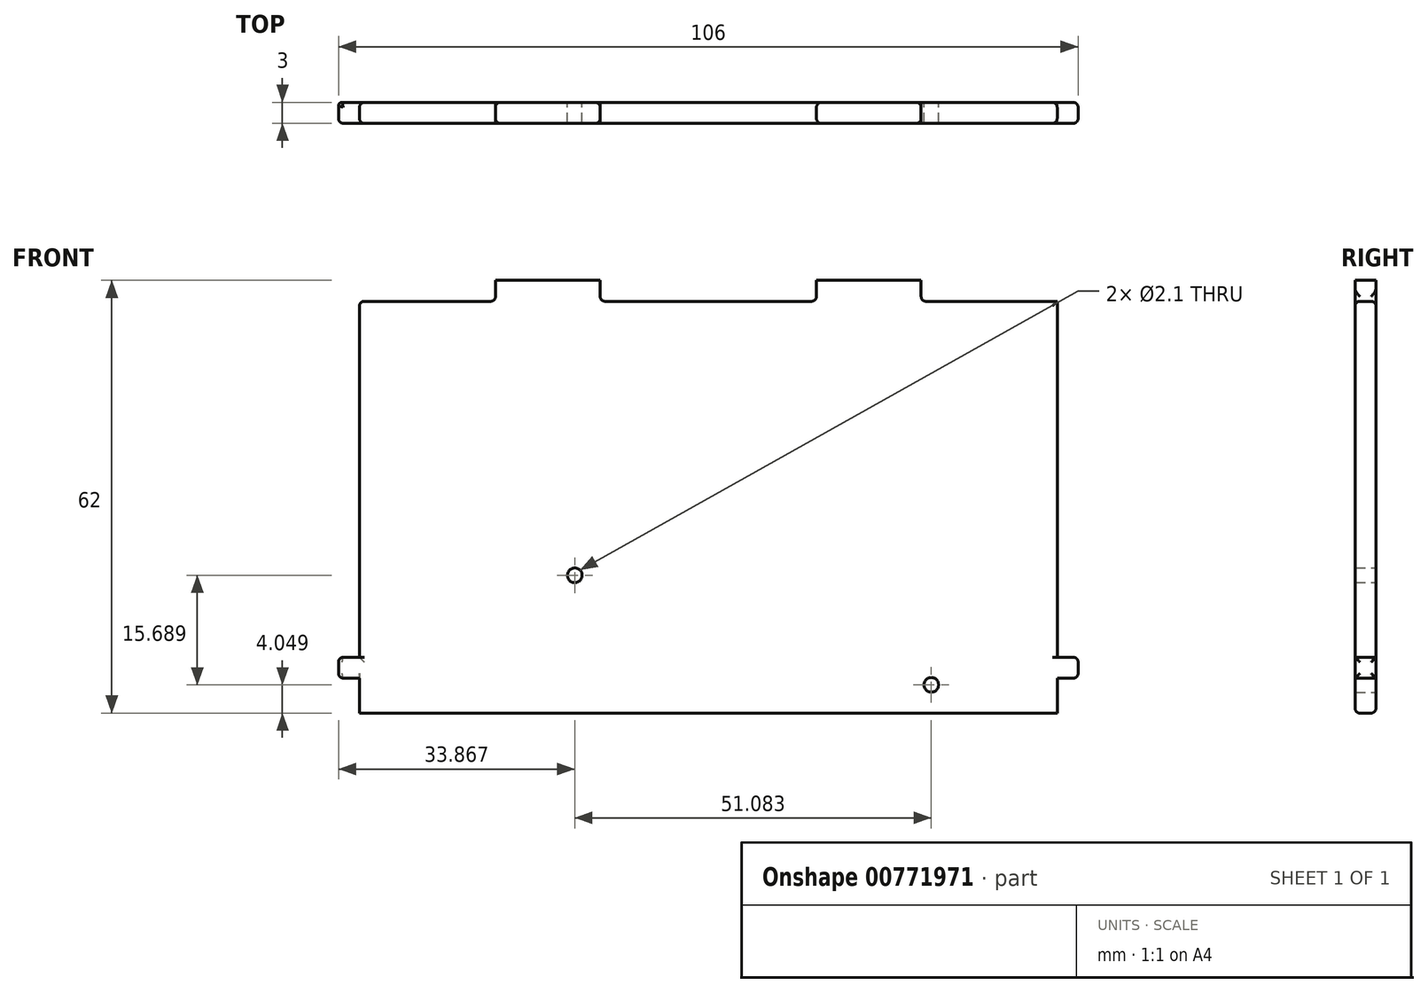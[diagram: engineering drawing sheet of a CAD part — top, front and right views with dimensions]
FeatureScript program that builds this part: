
annotation { "Feature Type Name" : "Feature", "Feature Type Description" : "" }
export const myFeature = defineFeature(function(context is Context, id is Id, definition is map)
    precondition{}
    {
        {
            var Q0;
            Q0=qCreatedBy(makeId("Front.planeOp"),FACE);
            var sketch = newSketch(context, id + "F0", { "sketchPlane" : qUnion([Q0])});
            skLineSegment(sketch, "E0.bottom", {"start": v(-50, -31.32) * mm, "end": v(50, -31.32) * mm});
            skLineSegment(sketch, "E0.top", {"start": v(-50, 27.68) * mm, "end": v(50, 27.68) * mm});
            skLineSegment(sketch, "E0.left", {"start": v(-50, -31.32) * mm, "end": v(-50, 27.68) * mm});
            skLineSegment(sketch, "E0.right", {"start": v(50, -31.32) * mm, "end": v(50, 27.68) * mm});
            skPoint(sketch, "E0.middle", {"position": v(0, -1.82) * mm});
            skLineSegment(sketch, "E1.bottom", {"start": v(-30.5, 27.68) * mm, "end": v(-15.5, 27.68) * mm});
            skLineSegment(sketch, "E1.top", {"start": v(-30.5, 30.68) * mm, "end": v(-15.5, 30.68) * mm});
            skLineSegment(sketch, "E1.left", {"start": v(-30.5, 27.68) * mm, "end": v(-30.5, 30.68) * mm});
            skLineSegment(sketch, "E1.right", {"start": v(-15.5, 27.68) * mm, "end": v(-15.5, 30.68) * mm});
            skLineSegment(sketch, "E2.bottom", {"start": v(30.5, 27.68) * mm, "end": v(15.5, 27.68) * mm});
            skLineSegment(sketch, "E2.top", {"start": v(30.5, 30.68) * mm, "end": v(15.5, 30.68) * mm});
            skLineSegment(sketch, "E2.left", {"start": v(30.5, 27.68) * mm, "end": v(30.5, 30.68) * mm});
            skLineSegment(sketch, "E2.right", {"start": v(15.5, 27.68) * mm, "end": v(15.5, 30.68) * mm});
            skLineSegment(sketch, "E3.bottom", {"start": v(-50, -23.32) * mm, "end": v(-53, -23.32) * mm});
            skLineSegment(sketch, "E3.top", {"start": v(-50, -26.32) * mm, "end": v(-53, -26.32) * mm});
            skLineSegment(sketch, "E3.left", {"start": v(-50, -23.32) * mm, "end": v(-50, -26.32) * mm});
            skLineSegment(sketch, "E3.right", {"start": v(-53, -23.32) * mm, "end": v(-53, -26.32) * mm});
            skLineSegment(sketch, "E4.bottom", {"start": v(50, -26.32) * mm, "end": v(53, -26.32) * mm});
            skLineSegment(sketch, "E4.top", {"start": v(50, -23.32) * mm, "end": v(53, -23.32) * mm});
            skLineSegment(sketch, "E4.left", {"start": v(50, -26.32) * mm, "end": v(50, -23.32) * mm});
            skLineSegment(sketch, "E4.right", {"start": v(53, -26.32) * mm, "end": v(53, -23.32) * mm});
            skCircle(sketch, "E5", {"center": v(31.95, -27.27) * mm, "radius": 1.05 * mm});
            skPoint(sketch, "E5.first.point", {"position": v(32.87, -27.78) * mm});
            skPoint(sketch, "E5.second.point", {"position": v(31.97, -26.22) * mm});
            skPoint(sketch, "E5.third.point", {"position": v(30.99, -27.7) * mm});
            skCircle(sketch, "E6", {"center": v(-19.13, -11.58) * mm, "radius": 1.05 * mm});
            skPoint(sketch, "E6.first.point", {"position": v(-20, -12.17) * mm});
            skPoint(sketch, "E6.second.point", {"position": v(-19.58, -12.53) * mm});
            skPoint(sketch, "E6.third.point", {"position": v(-18.39, -12.32) * mm});
            skSolve(sketch);
        }
        {
            var Q0;
            {var subQ7=sQuery(id+"F0.wireOp",EDGE,"E0.bottom");Q0=makeQuery(id+"F0.imprint","IMPRINT",FACE,{"disambiguationData":[TD([[makeQuery(id+"F0.imprint","IMPRINT",EDGE,{"derivedFrom":subQ7}),1.0]])]});}
            var Q1;
            {var subQ2=sQuery(id+"F0.wireOp",EDGE,"E4.bottom");Q1=makeQuery(id+"F0.imprint","IMPRINT",FACE,{"disambiguationData":[TD([[makeQuery(id+"F0.imprint","IMPRINT",EDGE,{"derivedFrom":subQ2}),1.0]])]});}
            var Q2;
            Q2=makeQuery(id+"F0.imprint","IMPRINT",FACE,{"disambiguationData":[TD([[makeQuery(id+"F0.imprint","IMPRINT",EDGE,{"derivedFrom":sQuery(id+"F0.wireOp",EDGE,"E2.top")}),1.0]])]});
            var Q3;
            Q3=makeQuery(id+"F0.imprint","IMPRINT",FACE,{"disambiguationData":[TD([[makeQuery(id+"F0.imprint","IMPRINT",EDGE,{"derivedFrom":sQuery(id+"F0.wireOp",EDGE,"E1.top")}),-1.0]])]});
            var Q4;
            {var subQ0=sQuery(id+"F0.wireOp",EDGE,"E3.bottom");Q4=makeQuery(id+"F0.imprint","IMPRINT",FACE,{"disambiguationData":[TD([[makeQuery(id+"F0.imprint","IMPRINT",EDGE,{"derivedFrom":subQ0}),1.0]])]});}
            extrude(context, id + "F1", {"entities" : qUnion([Q0, Q1, Q2, Q3, Q4]), "depth" : 3 * mm, "offsetDistance" : 25 * mm});
        }
        {
            var Q0;
            Q0=makeQuery(id+"F1.opExtrude","CAP_EDGE",EDGE,{"disambiguationData":[OSD([sQuery(id+"F0.wireOp",EDGE,"E3.right")])],"isStart":true});
            fillet(context, id + "F2", {"entities" : qUnion([Q0]), "radius" : 0.5 * mm, "tangentPropagation" : true, "allowEdgeOverflow" : false});
        }
        {
            var Q0;
            Q0=makeQuery(id+"F1.opExtrude","CAP_EDGE",EDGE,{"disambiguationData":[OSD([sQuery(id+"F0.wireOp",EDGE,"E3.right")])],"isStart":false});
            var Q1;
            Q1=makeQuery(id+"F1.opExtrude","SWEPT_EDGE",EDGE,{"disambiguationData":[OSD([sQuery(id+"F0.wireOp",EDGE,"E3.bottom"),sQuery(id+"F0.wireOp",EDGE,"E3.right")])]});
            var Q2;
            Q2=makeQuery(id+"F1.opExtrude","SWEPT_EDGE",EDGE,{"disambiguationData":[OSD([sQuery(id+"F0.wireOp",EDGE,"E3.top"),sQuery(id+"F0.wireOp",EDGE,"E3.right")])]});
            var Q3;
            {var subQ0=sQuery(id+"F0.wireOp",EDGE,"E3.right");Q3=makeQuery(id+"F2.opFillet","BLEND_EDGE",EDGE,{"blendedFrom":[makeQuery(id+"F1.opExtrude","CAP_EDGE",EDGE,{"disambiguationData":[OSD([subQ0])],"isStart":true}),makeQuery(id+"F1.opExtrude","SWEPT_FACE",FACE,{"disambiguationData":[OSD([subQ0])]})],"blendedInto":[makeQuery(id+"F1.opExtrude","SWEPT_FACE",FACE,{"disambiguationData":[OSD([subQ0])]})]});}
            var Q4;
            {var subQ0=sQuery(id+"F0.wireOp",EDGE,"E0.left");Q4=makeQuery(id+"F1.opExtrude","CAP_EDGE",EDGE,{"disambiguationData":[OSD([subQ0]),TDD([makeQuery(id+"F0.imprint","IMPRINT",EDGE,{"disambiguationData":[TD([[makeQuery(id+"F0.imprint","INTERSECT",VERTEX,{"derivedFrom":[subQ0,sQuery(id+"F0.wireOp",EDGE,"E3.bottom")]}),-1.0]])],"derivedFrom":subQ0})])],"isStart":true});}
            var Q5;
            {var subQ0=sQuery(id+"F0.wireOp",EDGE,"E0.left");Q5=makeQuery(id+"F1.opExtrude","CAP_EDGE",EDGE,{"disambiguationData":[OSD([subQ0]),TDD([makeQuery(id+"F0.imprint","IMPRINT",EDGE,{"disambiguationData":[TD([[makeQuery(id+"F0.imprint","INTERSECT",VERTEX,{"derivedFrom":[subQ0,sQuery(id+"F0.wireOp",EDGE,"E3.bottom")]}),-1.0]])],"derivedFrom":subQ0})])],"isStart":false});}
            var Q6;
            Q6=makeQuery(id+"F1.opExtrude","SWEPT_EDGE",EDGE,{"disambiguationData":[OSD([sQuery(id+"F0.wireOp",EDGE,"E0.top"),sQuery(id+"F0.wireOp",EDGE,"E0.left")])]});
            var Q7;
            {var subQ0=sQuery(id+"F0.wireOp",EDGE,"E0.top");Q7=makeQuery(id+"F1.opExtrude","CAP_EDGE",EDGE,{"disambiguationData":[OSD([subQ0]),TDD([makeQuery(id+"F0.imprint","IMPRINT",EDGE,{"disambiguationData":[TD([[makeQuery(id+"F0.imprint","INTERSECT",VERTEX,{"derivedFrom":[subQ0,sQuery(id+"F0.wireOp",EDGE,"E1.left")]}),1.0]])],"derivedFrom":subQ0})])],"isStart":true});}
            var Q8;
            {var subQ0=sQuery(id+"F0.wireOp",EDGE,"E0.top");Q8=makeQuery(id+"F1.opExtrude","CAP_EDGE",EDGE,{"disambiguationData":[OSD([subQ0]),TDD([makeQuery(id+"F0.imprint","IMPRINT",EDGE,{"disambiguationData":[TD([[makeQuery(id+"F0.imprint","INTERSECT",VERTEX,{"derivedFrom":[subQ0,sQuery(id+"F0.wireOp",EDGE,"E1.left")]}),1.0]])],"derivedFrom":subQ0})])],"isStart":false});}
            var Q9;
            Q9=makeQuery(id+"F1.opExtrude","SWEPT_EDGE",EDGE,{"disambiguationData":[OSD([sQuery(id+"F0.wireOp",EDGE,"E0.top"),sQuery(id+"F0.wireOp",EDGE,"E1.left")])]});
            var Q10;
            Q10=makeQuery(id+"F1.opExtrude","SWEPT_EDGE",EDGE,{"disambiguationData":[OSD([sQuery(id+"F0.wireOp",EDGE,"E0.top"),sQuery(id+"F0.wireOp",EDGE,"E1.right")])]});
            var Q11;
            {var subQ0=sQuery(id+"F0.wireOp",EDGE,"E0.top");Q11=makeQuery(id+"F1.opExtrude","CAP_EDGE",EDGE,{"disambiguationData":[OSD([subQ0]),TDD([makeQuery(id+"F0.imprint","IMPRINT",EDGE,{"disambiguationData":[TD([[makeQuery(id+"F0.imprint","INTERSECT",VERTEX,{"derivedFrom":[subQ0,sQuery(id+"F0.wireOp",EDGE,"E1.right")]}),-1.0]])],"derivedFrom":subQ0})])],"isStart":true});}
            var Q12;
            {var subQ0=sQuery(id+"F0.wireOp",EDGE,"E0.top");Q12=makeQuery(id+"F1.opExtrude","CAP_EDGE",EDGE,{"disambiguationData":[OSD([subQ0]),TDD([makeQuery(id+"F0.imprint","IMPRINT",EDGE,{"disambiguationData":[TD([[makeQuery(id+"F0.imprint","INTERSECT",VERTEX,{"derivedFrom":[subQ0,sQuery(id+"F0.wireOp",EDGE,"E1.right")]}),-1.0]])],"derivedFrom":subQ0})])],"isStart":false});}
            var Q13;
            {var subQ0=sQuery(id+"F0.wireOp",EDGE,"E0.top");Q13=makeQuery(id+"F1.opExtrude","CAP_EDGE",EDGE,{"disambiguationData":[OSD([subQ0]),TDD([makeQuery(id+"F0.imprint","IMPRINT",EDGE,{"disambiguationData":[TD([[makeQuery(id+"F0.imprint","INTERSECT",VERTEX,{"derivedFrom":[subQ0,sQuery(id+"F0.wireOp",EDGE,"E2.left")]}),-1.0]])],"derivedFrom":subQ0})])],"isStart":false});}
            var Q14;
            {var subQ0=sQuery(id+"F0.wireOp",EDGE,"E0.top");Q14=makeQuery(id+"F1.opExtrude","CAP_EDGE",EDGE,{"disambiguationData":[OSD([subQ0]),TDD([makeQuery(id+"F0.imprint","IMPRINT",EDGE,{"disambiguationData":[TD([[makeQuery(id+"F0.imprint","INTERSECT",VERTEX,{"derivedFrom":[subQ0,sQuery(id+"F0.wireOp",EDGE,"E2.left")]}),-1.0]])],"derivedFrom":subQ0})])],"isStart":true});}
            var Q15;
            Q15=makeQuery(id+"F1.opExtrude","SWEPT_EDGE",EDGE,{"disambiguationData":[OSD([sQuery(id+"F0.wireOp",EDGE,"E0.top"),sQuery(id+"F0.wireOp",EDGE,"E2.left")])]});
            var Q16;
            {var subQ0=sQuery(id+"F0.wireOp",EDGE,"E0.right");Q16=makeQuery(id+"F1.opExtrude","CAP_EDGE",EDGE,{"disambiguationData":[OSD([subQ0]),TDD([makeQuery(id+"F0.imprint","IMPRINT",EDGE,{"disambiguationData":[TD([[makeQuery(id+"F0.imprint","INTERSECT",VERTEX,{"derivedFrom":[subQ0,sQuery(id+"F0.wireOp",EDGE,"E4.top")]}),-1.0]])],"derivedFrom":subQ0})])],"isStart":false});}
            var Q17;
            {var subQ0=sQuery(id+"F0.wireOp",EDGE,"E0.right");Q17=makeQuery(id+"F1.opExtrude","CAP_EDGE",EDGE,{"disambiguationData":[OSD([subQ0]),TDD([makeQuery(id+"F0.imprint","IMPRINT",EDGE,{"disambiguationData":[TD([[makeQuery(id+"F0.imprint","INTERSECT",VERTEX,{"derivedFrom":[subQ0,sQuery(id+"F0.wireOp",EDGE,"E4.top")]}),-1.0]])],"derivedFrom":subQ0})])],"isStart":true});}
            var Q18;
            Q18=makeQuery(id+"F1.opExtrude","CAP_EDGE",EDGE,{"disambiguationData":[OSD([sQuery(id+"F0.wireOp",EDGE,"E4.right")])],"isStart":false});
            var Q19;
            Q19=makeQuery(id+"F1.opExtrude","SWEPT_EDGE",EDGE,{"disambiguationData":[OSD([sQuery(id+"F0.wireOp",EDGE,"E4.top"),sQuery(id+"F0.wireOp",EDGE,"E4.right")])]});
            var Q20;
            Q20=makeQuery(id+"F1.opExtrude","CAP_EDGE",EDGE,{"disambiguationData":[OSD([sQuery(id+"F0.wireOp",EDGE,"E4.right")])],"isStart":true});
            var Q21;
            Q21=makeQuery(id+"F1.opExtrude","SWEPT_EDGE",EDGE,{"disambiguationData":[OSD([sQuery(id+"F0.wireOp",EDGE,"E4.bottom"),sQuery(id+"F0.wireOp",EDGE,"E4.right")])]});
            var Q22;
            Q22=makeQuery(id+"F1.opExtrude","CAP_EDGE",EDGE,{"disambiguationData":[OSD([sQuery(id+"F0.wireOp",EDGE,"E0.bottom")])],"isStart":false});
            var Q23;
            Q23=makeQuery(id+"F1.opExtrude","CAP_EDGE",EDGE,{"disambiguationData":[OSD([sQuery(id+"F0.wireOp",EDGE,"E0.bottom")])],"isStart":true});
            var Q24;
            Q24=makeQuery(id+"F1.opExtrude","CAP_EDGE",EDGE,{"disambiguationData":[OSD([sQuery(id+"F0.wireOp",EDGE,"E2.right")])],"isStart":false});
            var Q25;
            Q25=makeQuery(id+"F1.opExtrude","CAP_EDGE",EDGE,{"disambiguationData":[OSD([sQuery(id+"F0.wireOp",EDGE,"E2.right")])],"isStart":true});
            var Q26;
            Q26=makeQuery(id+"F1.opExtrude","SWEPT_EDGE",EDGE,{"disambiguationData":[OSD([sQuery(id+"F0.wireOp",EDGE,"E0.top"),sQuery(id+"F0.wireOp",EDGE,"E2.right")])]});
            fillet(context, id + "F3", {"entities" : qUnion([Q0, Q1, Q2, Q3, Q4, Q5, Q6, Q7, Q8, Q9, Q10, Q11, Q12, Q13, Q14, Q15, Q16, Q17, Q18, Q19, Q20, Q21, Q22, Q23, Q24, Q25, Q26]), "radius" : 0.7 * mm, "tangentPropagation" : true, "allowEdgeOverflow" : false});
        }
    });
